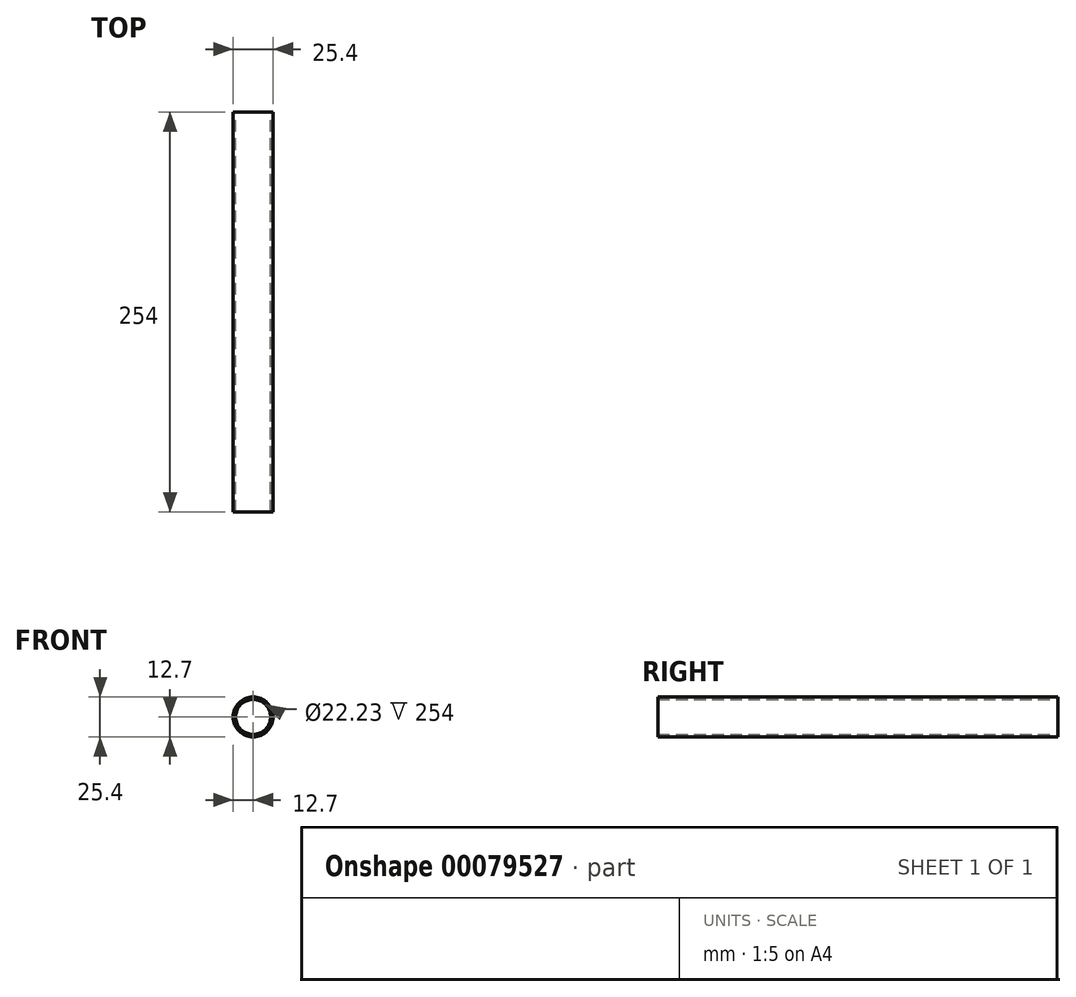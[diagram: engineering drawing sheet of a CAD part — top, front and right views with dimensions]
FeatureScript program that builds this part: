
annotation { "Feature Type Name" : "Feature", "Feature Type Description" : "" }
export const myFeature = defineFeature(function(context is Context, id is Id, definition is map)
    precondition{}
    {
        {
            var Q0;
            Q0=qCreatedBy(makeId("Front.planeOp"),FACE);
            var sketch = newSketch(context, id + "F0", { "sketchPlane" : qUnion([Q0])});
            skCircle(sketch, "E0", {"center": v(0, 0) * mm, "radius": 12.7 * mm});
            skCircle(sketch, "E1", {"center": v(0, 0) * mm, "radius": 11.11 * mm});
            skSolve(sketch);
        }
        {
            var Q0;
            Q0=makeQuery(id+"F0.imprint","IMPRINT",FACE,{"disambiguationData":[TD([[makeQuery(id+"F0.imprint","IMPRINT",EDGE,{"derivedFrom":sQuery(id+"F0.wireOp",EDGE,"E0")}),1.0]])]});
            extrude(context, id + "F1", {"entities" : qUnion([Q0]), "depth" : 254 * mm});
        }
    });
